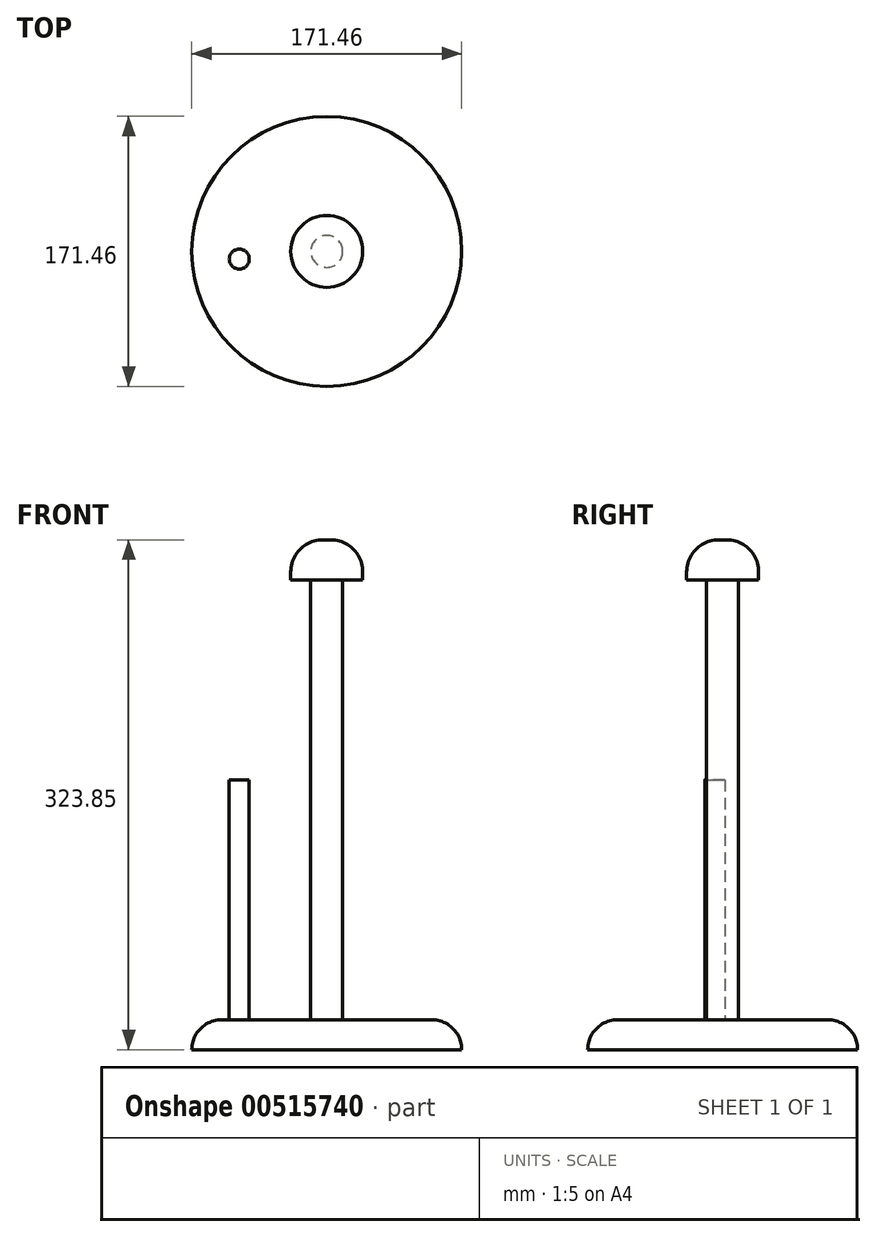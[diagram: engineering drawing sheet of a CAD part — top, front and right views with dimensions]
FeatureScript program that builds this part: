
annotation { "Feature Type Name" : "Feature", "Feature Type Description" : "" }
export const myFeature = defineFeature(function(context is Context, id is Id, definition is map)
    precondition{}
    {
        {
            var Q0;
            Q0=qCreatedBy(makeId("Top.planeOp"),FACE);
            var sketch = newSketch(context, id + "F0", { "sketchPlane" : qUnion([Q0])});
            skCircle(sketch, "E0", {"center": v(0, 0) * mm, "radius": 85.73 * mm});
            skSolve(sketch);
        }
        {
            var Q0;
            Q0 = qSketchRegion(id + "F0", true);
            extrude(context, id + "F1", {"entities" : qUnion([Q0]), "depth" : 19.05 * mm, "offsetDistance" : 25.4 * mm});
        }
        {
            var Q0;
            Q0=makeQuery(id+"F1.opExtrude","CAP_EDGE",EDGE,{"disambiguationData":[OSD([sQuery(id+"F0.wireOp",EDGE,"E0")])],"isStart":false});
            fillet(context, id + "F2", {"entities" : qUnion([Q0]), "radius" : 19.05 * mm, "tangentPropagation" : true, "allowEdgeOverflow" : false});
        }
        {
            var Q0;
            Q0=makeQuery(id+"F1.opExtrude","CAP_FACE",FACE,{"disambiguationData":[OSD([sQuery(id+"F0.wireOp",EDGE,"E0")])],"isStart":false});
            var sketch = newSketch(context, id + "F3", { "sketchPlane" : qUnion([Q0])});
            skCircle(sketch, "E1", {"center": v(0, 0) * mm, "radius": 10.16 * mm});
            skSolve(sketch);
        }
        {
            var Q0;
            Q0 = qSketchRegion(id + "F3", true);
            extrude(context, id + "F4", {"entities" : qUnion([Q0]), "operationType" : NewBodyOperationType.ADD, "depth" : 279.4 * mm, "offsetDistance" : 25.4 * mm});
        }
        {
            var Q0;
            Q0=makeQuery(id+"F4.opExtrude","CAP_FACE",FACE,{"disambiguationData":[OSD([sQuery(id+"F3.wireOp",EDGE,"E1")])],"isStart":false});
            var sketch = newSketch(context, id + "F5", { "sketchPlane" : qUnion([Q0])});
            skCircle(sketch, "E2", {"center": v(0, 0) * mm, "radius": 22.86 * mm});
            skSolve(sketch);
        }
        {
            var Q0;
            Q0 = qSketchRegion(id + "F5", true);
            extrude(context, id + "F6", {"entities" : qUnion([Q0]), "operationType" : NewBodyOperationType.ADD, "depth" : 25.4 * mm, "offsetDistance" : 25.4 * mm});
        }
        {
            var Q0;
            Q0=makeQuery(id+"F6.opExtrude","CAP_EDGE",EDGE,{"disambiguationData":[OSD([sQuery(id+"F5.wireOp",EDGE,"E2")])],"isStart":false});
            fillet(context, id + "F7", {"entities" : qUnion([Q0]), "radius" : 20.32 * mm, "tangentPropagation" : true, "allowEdgeOverflow" : false});
        }
        {
            var Q0;
            Q0=makeQuery(id+"F1.opExtrude","CAP_FACE",FACE,{"disambiguationData":[OSD([sQuery(id+"F0.wireOp",EDGE,"E0")])],"isStart":false});
            var sketch = newSketch(context, id + "F8", { "sketchPlane" : qUnion([Q0])});
            skCircle(sketch, "E3", {"center": v(-55.56, -4.9) * mm, "radius": 6.35 * mm});
            skSolve(sketch);
        }
        {
            var Q0;
            Q0 = qSketchRegion(id + "F8", true);
            extrude(context, id + "F9", {"entities" : qUnion([Q0]), "operationType" : NewBodyOperationType.ADD, "depth" : 152.4 * mm, "offsetDistance" : 25.4 * mm});
        }
    });
